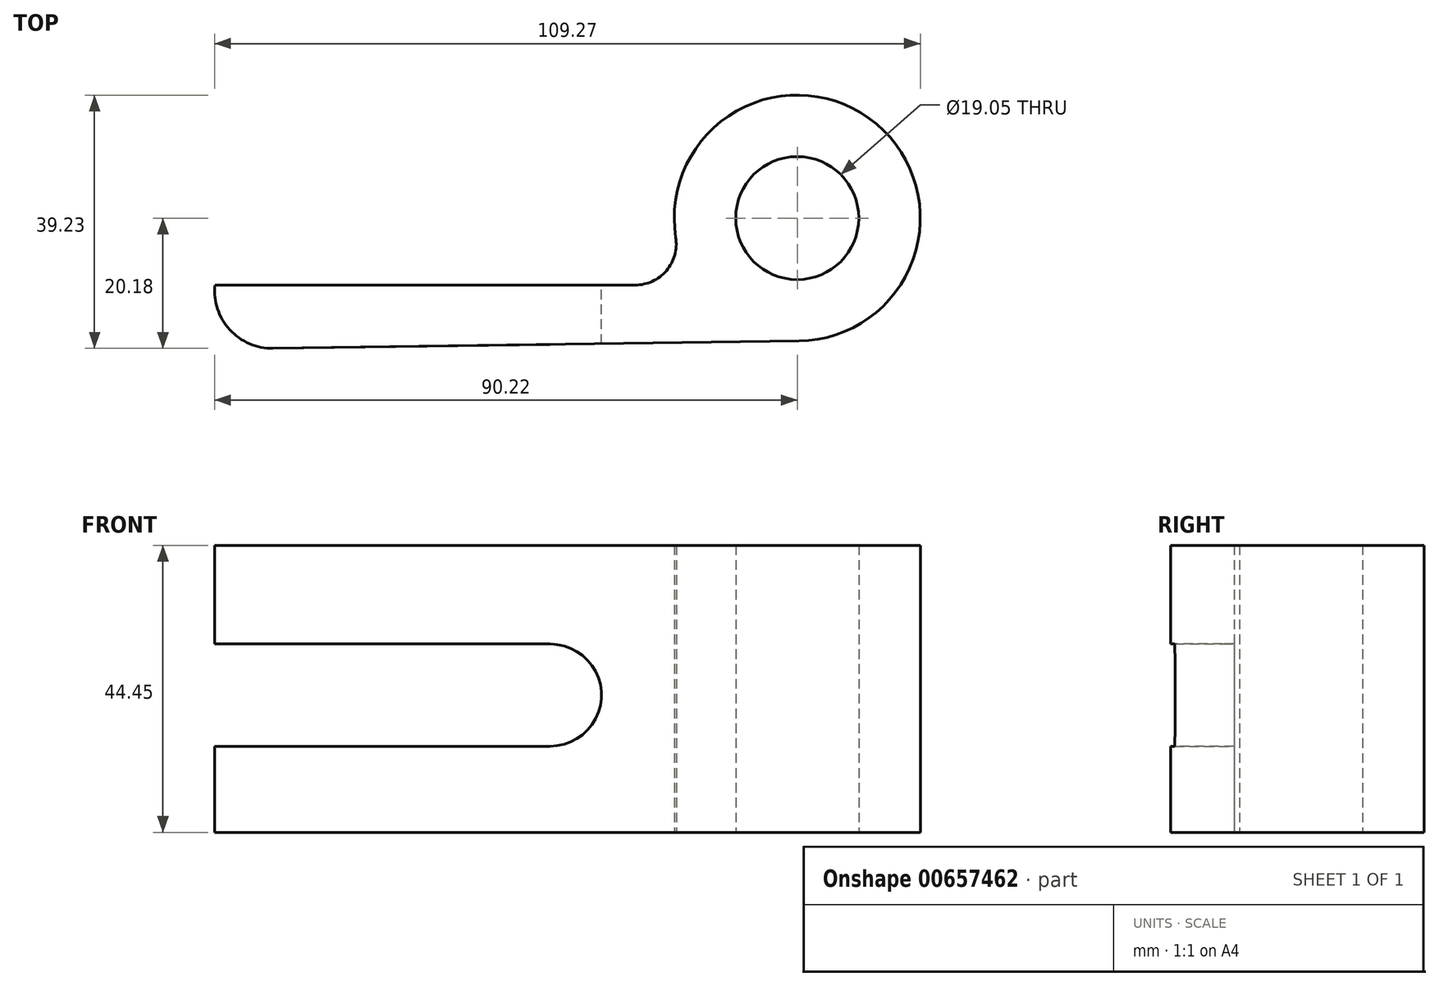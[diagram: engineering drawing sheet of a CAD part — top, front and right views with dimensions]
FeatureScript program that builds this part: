
annotation { "Feature Type Name" : "Feature", "Feature Type Description" : "" }
export const myFeature = defineFeature(function(context is Context, id is Id, definition is map)
    precondition{}
    {
        {
            var Q0;
            Q0=qCreatedBy(makeId("Top.planeOp"),FACE);
            var sketch = newSketch(context, id + "F0", { "sketchPlane" : qUnion([Q0])});
            skArc(sketch, "E0", {"start": v(0.27, -19.05) * mm, "mid": v(12.26, 14.58) * mm, "end": v(-18.8, -3.02) * mm});
            skLineSegment(sketch, "E1", {"start": v(-25.08, -10.37) * mm, "end": v(-35.65, -10.37) * mm});
            skLineSegment(sketch, "E2", {"start": v(-35.65, -10.37) * mm, "end": v(-78.48, -10.37) * mm});
            skPoint(sketch, "E3.visualSharp", {"position": v(-15.98, -10.37) * mm});
            skArc(sketch, "E3.filletArc", {"start": v(-25.08, -10.37) * mm, "mid": v(-20.25, -8.14) * mm, "end": v(-18.8, -3.02) * mm});
            skLineSegment(sketch, "E4", {"start": v(0.27, -19.05) * mm, "end": v(-81.16, -20.18) * mm});
            skLineSegment(sketch, "E5", {"start": v(-78.48, -10.37) * mm, "end": v(-81.14, -10.37) * mm});
            skPoint(sketch, "E6.center.orphan", {"position": v(-81.14, -15) * mm});
            skArc(sketch, "E7", {"start": v(-81.14, -10.37) * mm, "mid": v(-81.2, -10.38) * mm, "end": v(-81.28, -10.38) * mm});
            skLineSegment(sketch, "E8", {"start": v(-81.14, -10.37) * mm, "end": v(-81.28, -10.38) * mm});
            skLineSegment(sketch, "E9", {"start": v(-81.14, -10.37) * mm, "end": v(-90.17, -10.37) * mm});
            skArc(sketch, "E10", {"start": v(-90.17, -10.37) * mm, "mid": v(-87.86, -17.3) * mm, "end": v(-81.16, -20.18) * mm});
            skSolve(sketch);
        }
        {
            var Q0;
            Q0 = qSketchRegion(id + "F0", true);
            extrude(context, id + "F1", {"entities" : qUnion([Q0]), "depth" : 44.45 * mm, "offsetDistance" : 25.4 * mm});
        }
        {
            var Q0;
            Q0=qCreatedBy(makeId("Top.planeOp"),FACE);
            var sketch = newSketch(context, id + "F2", { "sketchPlane" : qUnion([Q0])});
            skCircle(sketch, "E11", {"center": v(0, 0) * mm, "radius": 9.53 * mm});
            skSolve(sketch);
        }
        {
            var Q0;
            Q0 = qSketchRegion(id + "F2", true);
            extrude(context, id + "F3", {"entities" : qUnion([Q0]), "operationType" : NewBodyOperationType.REMOVE, "depth" : 50.8 * mm, "offsetDistance" : 25.4 * mm});
        }
        {
            var Q0;
            Q0=makeQuery(id+"F1.opExtrude","SWEPT_FACE",FACE,{"disambiguationData":[OSD([sQuery(id+"F0.wireOp",EDGE,"E1"),sQuery(id+"F0.wireOp",EDGE,"E2")])]});
            var sketch = newSketch(context, id + "F4", { "sketchPlane" : qUnion([Q0])});
            skLineSegment(sketch, "E12.bottom", {"start": v(77.26, 13.32) * mm, "end": v(38.23, 13.32) * mm});
            skLineSegment(sketch, "E12.top", {"start": v(77.26, 29.2) * mm, "end": v(38.23, 29.2) * mm});
            skLineSegment(sketch, "E12.left", {"start": v(77.26, 13.32) * mm, "end": v(77.26, 29.2) * mm});
            skLineSegment(sketch, "E13", {"start": v(77.26, 13.32) * mm, "end": v(86.62, 13.32) * mm});
            skLineSegment(sketch, "E14", {"start": v(86.62, 13.32) * mm, "end": v(86.62, 29.2) * mm});
            skLineSegment(sketch, "E15", {"start": v(86.62, 29.2) * mm, "end": v(77.26, 29.2) * mm});
            skArc(sketch, "E16", {"start": v(38.23, 29.2) * mm, "mid": v(30.3, 21.26) * mm, "end": v(38.23, 13.32) * mm});
            skLineSegment(sketch, "E17", {"start": v(86.62, 13.32) * mm, "end": v(90.17, 13.32) * mm});
            skLineSegment(sketch, "E18", {"start": v(90.17, 29.2) * mm, "end": v(86.62, 29.2) * mm});
            skLineSegment(sketch, "E19", {"start": v(86.62, 13.32) * mm, "end": v(98.24, 13.32) * mm});
            skLineSegment(sketch, "E20", {"start": v(98.24, 13.32) * mm, "end": v(98.24, 28.88) * mm});
            skLineSegment(sketch, "E21", {"start": v(98.24, 28.88) * mm, "end": v(90.17, 29.2) * mm});
            skSolve(sketch);
        }
        {
            var Q0;
            Q0 = qSketchRegion(id + "F4", true);
            extrude(context, id + "F5", {"entities" : qUnion([Q0]), "operationType" : NewBodyOperationType.REMOVE, "oppositeDirection" : true, "depth" : 50.8 * mm, "offsetDistance" : 25.4 * mm});
        }
    });
